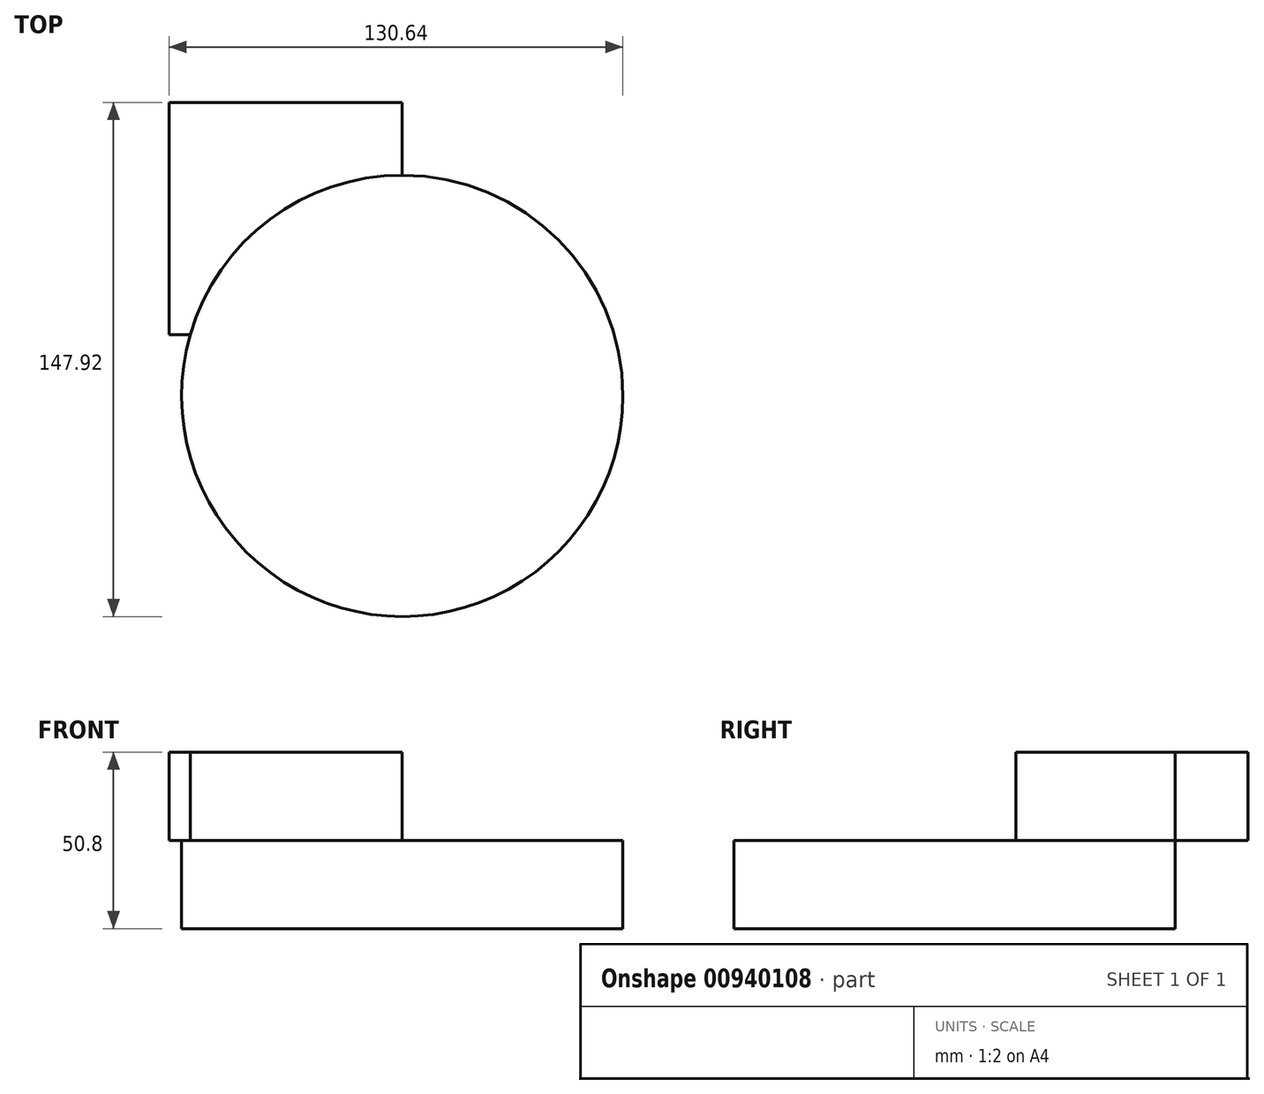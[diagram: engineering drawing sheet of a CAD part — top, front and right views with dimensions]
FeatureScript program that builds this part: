
annotation { "Feature Type Name" : "Feature", "Feature Type Description" : "" }
export const myFeature = defineFeature(function(context is Context, id is Id, definition is map)
    precondition{}
    {
        {
            var Q0;
            Q0=qCreatedBy(makeId("Top.planeOp"),FACE);
            var sketch = newSketch(context, id + "F0", { "sketchPlane" : qUnion([Q0])});
            skCircle(sketch, "E0", {"center": v(0, 0) * mm, "radius": 63.5 * mm});
            skSolve(sketch);
        }
        {
            var Q0;
            Q0=makeQuery(id+"F0.imprint","IMPRINT",FACE,{"disambiguationData":[TD([[makeQuery(id+"F0.imprint","IMPRINT",EDGE,{"derivedFrom":sQuery(id+"F0.wireOp",EDGE,"E0")}),1.0]])]});
            extrude(context, id + "F1", {"entities" : qUnion([Q0]), "depth" : 25.4 * mm, "offsetDistance" : 25.4 * mm});
        }
        {
            var Q0;
            Q0=makeQuery(id+"F1.opExtrude","CAP_FACE",FACE,{"disambiguationData":[OSD([sQuery(id+"F0.wireOp",EDGE,"E0")])],"isStart":false});
            var sketch = newSketch(context, id + "F2", { "sketchPlane" : qUnion([Q0])});
            skLineSegment(sketch, "E1.bottom", {"start": v(-67.14, 84.42) * mm, "end": v(0, 84.42) * mm});
            skLineSegment(sketch, "E1.top", {"start": v(-67.14, 17.62) * mm, "end": v(0, 17.62) * mm});
            skLineSegment(sketch, "E1.left", {"start": v(-67.14, 84.42) * mm, "end": v(-67.14, 17.62) * mm});
            skLineSegment(sketch, "E1.right", {"start": v(0, 84.42) * mm, "end": v(0, 17.62) * mm});
            skSolve(sketch);
        }
        {
            var Q0;
            {var subQ1=sQuery(id+"F2.wireOp",EDGE,"E1.bottom");Q0=makeQuery(id+"F2.imprint","IMPRINT",FACE,{"disambiguationData":[TD([[makeQuery(id+"F2.imprint","IMPRINT",EDGE,{"derivedFrom":subQ1}),-1.0]])]});}
            extrude(context, id + "F3", {"entities" : qUnion([Q0]), "depth" : 25.4 * mm, "offsetDistance" : 25.4 * mm});
        }
    });
